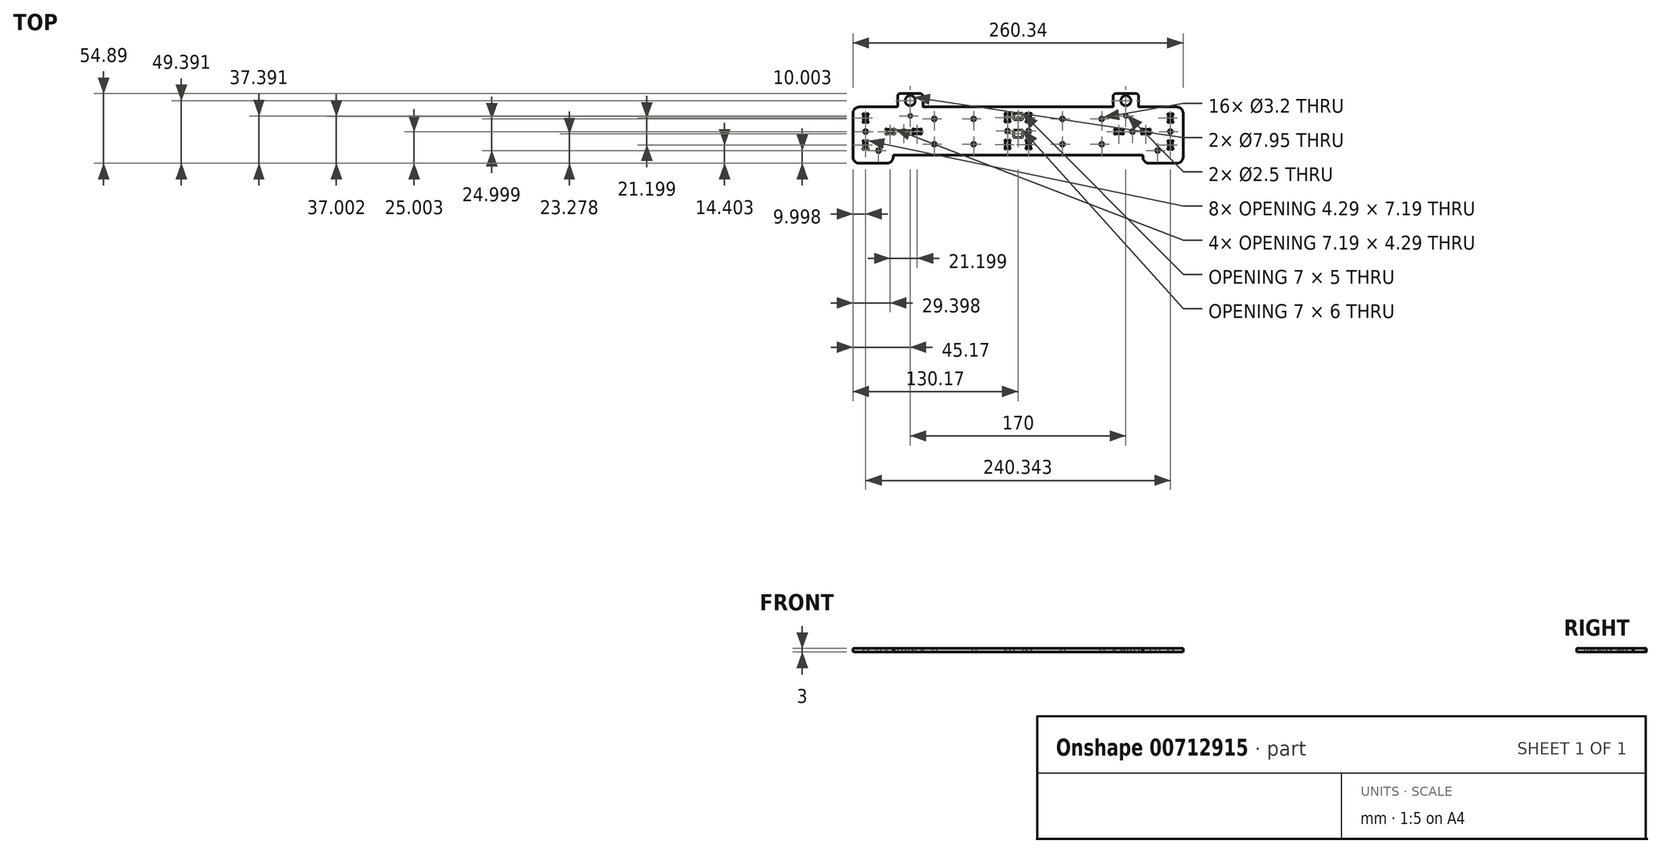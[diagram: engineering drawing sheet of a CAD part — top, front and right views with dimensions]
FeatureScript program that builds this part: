
annotation { "Feature Type Name" : "Feature", "Feature Type Description" : "" }
export const myFeature = defineFeature(function(context is Context, id is Id, definition is map)
    precondition{}
    {
        {
            var Q0;
            Q0=qCreatedBy(makeId("Top.planeOp"),FACE);
            var sketch = newSketch(context, id + "F0", { "sketchPlane" : qUnion([Q0])});
            skArc(sketch, "E0", {"start": v(-130.17, -20.39) * mm, "mid": v(-128.7, -23.92) * mm, "end": v(-125.17, -25.39) * mm});
            skLineSegment(sketch, "E1", {"start": v(-130.17, -20.39) * mm, "end": v(-130.17, 14) * mm});
            skArc(sketch, "E2", {"start": v(-125.17, 19) * mm, "mid": v(-128.7, 17.54) * mm, "end": v(-130.17, 14) * mm});
            skLineSegment(sketch, "E3", {"start": v(-125.17, 19) * mm, "end": v(-95.5, 19) * mm});
            skArc(sketch, "E4", {"start": v(-95.5, 19) * mm, "mid": v(-95.15, 19.15) * mm, "end": v(-95, 19.5) * mm});
            skArc(sketch, "E5", {"start": v(-75, 19.5) * mm, "mid": v(-74.85, 19.15) * mm, "end": v(-74.5, 19) * mm});
            skLineSegment(sketch, "E6", {"start": v(-74.5, 19) * mm, "end": v(74.5, 19) * mm});
            skArc(sketch, "E7", {"start": v(74.5, 19) * mm, "mid": v(74.85, 19.15) * mm, "end": v(75, 19.5) * mm});
            skArc(sketch, "E8", {"start": v(95, 19.5) * mm, "mid": v(95.15, 19.15) * mm, "end": v(95.5, 19) * mm});
            skLineSegment(sketch, "E9", {"start": v(95.5, 19) * mm, "end": v(125.17, 19) * mm});
            skArc(sketch, "E10", {"start": v(130.17, 14) * mm, "mid": v(128.7, 17.54) * mm, "end": v(125.17, 19) * mm});
            skLineSegment(sketch, "E11", {"start": v(130.17, 14) * mm, "end": v(130.17, -20.39) * mm});
            skArc(sketch, "E12", {"start": v(125.17, -25.39) * mm, "mid": v(128.7, -23.92) * mm, "end": v(130.17, -20.39) * mm});
            skArc(sketch, "E13", {"start": v(118.95, -7.64) * mm, "mid": v(119.14, -7.82) * mm, "end": v(119.39, -7.89) * mm});
            skArc(sketch, "E14", {"start": v(118.95, -7.64) * mm, "mid": v(118.17, -7.53) * mm, "end": v(118.27, -8.32) * mm});
            skArc(sketch, "E15", {"start": v(118.52, -8.75) * mm, "mid": v(118.45, -8.5) * mm, "end": v(118.27, -8.32) * mm});
            skLineSegment(sketch, "E16", {"start": v(118.52, -8.75) * mm, "end": v(118.52, -13.22) * mm});
            skArc(sketch, "E17", {"start": v(118.27, -13.65) * mm, "mid": v(118.45, -13.47) * mm, "end": v(118.52, -13.22) * mm});
            skArc(sketch, "E18", {"start": v(118.27, -13.65) * mm, "mid": v(118.17, -14.44) * mm, "end": v(118.95, -14.34) * mm});
            skArc(sketch, "E19", {"start": v(119.39, -14.09) * mm, "mid": v(119.14, -14.15) * mm, "end": v(118.95, -14.34) * mm});
            skLineSegment(sketch, "E20", {"start": v(119.39, -14.09) * mm, "end": v(120.96, -14.09) * mm});
            skArc(sketch, "E21", {"start": v(121.39, -14.34) * mm, "mid": v(121.2, -14.15) * mm, "end": v(120.96, -14.09) * mm});
            skArc(sketch, "E22", {"start": v(121.39, -14.34) * mm, "mid": v(122.17, -14.44) * mm, "end": v(122.07, -13.65) * mm});
            skArc(sketch, "E23", {"start": v(121.82, -13.22) * mm, "mid": v(121.89, -13.47) * mm, "end": v(122.07, -13.65) * mm});
            skLineSegment(sketch, "E24", {"start": v(121.82, -13.22) * mm, "end": v(121.82, -8.75) * mm});
            skArc(sketch, "E25", {"start": v(122.07, -8.32) * mm, "mid": v(121.89, -8.5) * mm, "end": v(121.82, -8.75) * mm});
            skArc(sketch, "E26", {"start": v(122.07, -8.32) * mm, "mid": v(122.17, -7.53) * mm, "end": v(121.39, -7.64) * mm});
            skArc(sketch, "E27", {"start": v(120.96, -7.89) * mm, "mid": v(121.2, -7.82) * mm, "end": v(121.39, -7.64) * mm});
            skLineSegment(sketch, "E28", {"start": v(120.96, -7.89) * mm, "end": v(119.39, -7.89) * mm});
            skArc(sketch, "E29", {"start": v(118.95, 13.56) * mm, "mid": v(119.14, 13.38) * mm, "end": v(119.39, 13.31) * mm});
            skArc(sketch, "E30", {"start": v(118.95, 13.56) * mm, "mid": v(118.17, 13.67) * mm, "end": v(118.27, 12.88) * mm});
            skArc(sketch, "E31", {"start": v(118.52, 12.45) * mm, "mid": v(118.45, 12.7) * mm, "end": v(118.27, 12.88) * mm});
            skLineSegment(sketch, "E32", {"start": v(118.52, 12.45) * mm, "end": v(118.52, 7.98) * mm});
            skArc(sketch, "E33", {"start": v(118.27, 7.55) * mm, "mid": v(118.45, 7.73) * mm, "end": v(118.52, 7.98) * mm});
            skArc(sketch, "E34", {"start": v(118.27, 7.55) * mm, "mid": v(118.17, 6.76) * mm, "end": v(118.95, 6.86) * mm});
            skArc(sketch, "E35", {"start": v(119.39, 7.11) * mm, "mid": v(119.14, 7.05) * mm, "end": v(118.95, 6.86) * mm});
            skLineSegment(sketch, "E36", {"start": v(119.39, 7.11) * mm, "end": v(120.96, 7.11) * mm});
            skArc(sketch, "E37", {"start": v(121.39, 6.86) * mm, "mid": v(121.2, 7.05) * mm, "end": v(120.96, 7.11) * mm});
            skArc(sketch, "E38", {"start": v(121.39, 6.86) * mm, "mid": v(122.17, 6.76) * mm, "end": v(122.07, 7.55) * mm});
            skArc(sketch, "E39", {"start": v(121.82, 7.98) * mm, "mid": v(121.89, 7.73) * mm, "end": v(122.07, 7.55) * mm});
            skLineSegment(sketch, "E40", {"start": v(121.82, 7.98) * mm, "end": v(121.82, 12.45) * mm});
            skArc(sketch, "E41", {"start": v(122.07, 12.88) * mm, "mid": v(121.89, 12.7) * mm, "end": v(121.82, 12.45) * mm});
            skArc(sketch, "E42", {"start": v(122.07, 12.88) * mm, "mid": v(122.17, 13.67) * mm, "end": v(121.39, 13.56) * mm});
            skArc(sketch, "E43", {"start": v(120.96, 13.31) * mm, "mid": v(121.2, 13.38) * mm, "end": v(121.39, 13.56) * mm});
            skLineSegment(sketch, "E44", {"start": v(120.96, 13.31) * mm, "end": v(119.39, 13.31) * mm});
            skArc(sketch, "E45", {"start": v(-119.39, -7.89) * mm, "mid": v(-119.14, -7.82) * mm, "end": v(-118.95, -7.64) * mm});
            skArc(sketch, "E46", {"start": v(-118.27, -8.32) * mm, "mid": v(-118.17, -7.53) * mm, "end": v(-118.95, -7.64) * mm});
            skArc(sketch, "E47", {"start": v(-118.27, -8.32) * mm, "mid": v(-118.45, -8.5) * mm, "end": v(-118.52, -8.75) * mm});
            skLineSegment(sketch, "E48", {"start": v(-118.52, -8.75) * mm, "end": v(-118.52, -13.22) * mm});
            skArc(sketch, "E49", {"start": v(-118.52, -13.22) * mm, "mid": v(-118.45, -13.47) * mm, "end": v(-118.27, -13.65) * mm});
            skArc(sketch, "E50", {"start": v(-118.95, -14.34) * mm, "mid": v(-118.17, -14.44) * mm, "end": v(-118.27, -13.65) * mm});
            skArc(sketch, "E51", {"start": v(-118.95, -14.34) * mm, "mid": v(-119.14, -14.15) * mm, "end": v(-119.39, -14.09) * mm});
            skLineSegment(sketch, "E52", {"start": v(-119.39, -14.09) * mm, "end": v(-120.96, -14.09) * mm});
            skArc(sketch, "E53", {"start": v(-120.96, -14.09) * mm, "mid": v(-121.2, -14.15) * mm, "end": v(-121.39, -14.34) * mm});
            skArc(sketch, "E54", {"start": v(-122.07, -13.65) * mm, "mid": v(-122.17, -14.44) * mm, "end": v(-121.39, -14.34) * mm});
            skArc(sketch, "E55", {"start": v(-122.07, -13.65) * mm, "mid": v(-121.89, -13.47) * mm, "end": v(-121.82, -13.22) * mm});
            skLineSegment(sketch, "E56", {"start": v(-121.82, -13.22) * mm, "end": v(-121.82, -8.75) * mm});
            skArc(sketch, "E57", {"start": v(-121.82, -8.75) * mm, "mid": v(-121.89, -8.5) * mm, "end": v(-122.07, -8.32) * mm});
            skArc(sketch, "E58", {"start": v(-121.39, -7.64) * mm, "mid": v(-122.17, -7.53) * mm, "end": v(-122.07, -8.32) * mm});
            skArc(sketch, "E59", {"start": v(-121.39, -7.64) * mm, "mid": v(-121.2, -7.82) * mm, "end": v(-120.96, -7.89) * mm});
            skLineSegment(sketch, "E60", {"start": v(-120.96, -7.89) * mm, "end": v(-119.39, -7.89) * mm});
            skArc(sketch, "E61", {"start": v(-119.39, 13.31) * mm, "mid": v(-119.14, 13.38) * mm, "end": v(-118.95, 13.56) * mm});
            skArc(sketch, "E62", {"start": v(-118.27, 12.88) * mm, "mid": v(-118.17, 13.67) * mm, "end": v(-118.95, 13.56) * mm});
            skArc(sketch, "E63", {"start": v(-118.27, 12.88) * mm, "mid": v(-118.45, 12.7) * mm, "end": v(-118.52, 12.45) * mm});
            skLineSegment(sketch, "E64", {"start": v(-118.52, 12.45) * mm, "end": v(-118.52, 7.98) * mm});
            skArc(sketch, "E65", {"start": v(-118.52, 7.98) * mm, "mid": v(-118.45, 7.73) * mm, "end": v(-118.27, 7.55) * mm});
            skArc(sketch, "E66", {"start": v(-118.95, 6.86) * mm, "mid": v(-118.17, 6.76) * mm, "end": v(-118.27, 7.55) * mm});
            skArc(sketch, "E67", {"start": v(-118.95, 6.86) * mm, "mid": v(-119.14, 7.05) * mm, "end": v(-119.39, 7.11) * mm});
            skLineSegment(sketch, "E68", {"start": v(-119.39, 7.11) * mm, "end": v(-120.96, 7.11) * mm});
            skArc(sketch, "E69", {"start": v(-120.96, 7.11) * mm, "mid": v(-121.2, 7.05) * mm, "end": v(-121.39, 6.86) * mm});
            skArc(sketch, "E70", {"start": v(-122.07, 7.55) * mm, "mid": v(-122.17, 6.76) * mm, "end": v(-121.39, 6.86) * mm});
            skArc(sketch, "E71", {"start": v(-122.07, 7.55) * mm, "mid": v(-121.89, 7.73) * mm, "end": v(-121.82, 7.98) * mm});
            skLineSegment(sketch, "E72", {"start": v(-121.82, 7.98) * mm, "end": v(-121.82, 12.45) * mm});
            skArc(sketch, "E73", {"start": v(-121.82, 12.45) * mm, "mid": v(-121.89, 12.7) * mm, "end": v(-122.07, 12.88) * mm});
            skArc(sketch, "E74", {"start": v(-121.39, 13.56) * mm, "mid": v(-122.17, 13.67) * mm, "end": v(-122.07, 12.88) * mm});
            skArc(sketch, "E75", {"start": v(-121.39, 13.56) * mm, "mid": v(-121.2, 13.38) * mm, "end": v(-120.96, 13.31) * mm});
            skLineSegment(sketch, "E76", {"start": v(-120.96, 13.31) * mm, "end": v(-119.39, 13.31) * mm});
            skCircle(sketch, "E77", {"center": v(120.17, -0.39) * mm, "radius": 1.6 * mm});
            skCircle(sketch, "E78", {"center": v(66, -10.39) * mm, "radius": 1.6 * mm});
            skCircle(sketch, "E79", {"center": v(66, 9.61) * mm, "radius": 1.6 * mm});
            skCircle(sketch, "E80", {"center": v(35, -10.39) * mm, "radius": 1.6 * mm});
            skCircle(sketch, "E81", {"center": v(35, 9.61) * mm, "radius": 1.6 * mm});
            skCircle(sketch, "E82", {"center": v(-35, -10.39) * mm, "radius": 1.6 * mm});
            skCircle(sketch, "E83", {"center": v(-35, 9.61) * mm, "radius": 1.6 * mm});
            skCircle(sketch, "E84", {"center": v(-66, -10.39) * mm, "radius": 1.6 * mm});
            skCircle(sketch, "E85", {"center": v(-66, 9.61) * mm, "radius": 1.6 * mm});
            skCircle(sketch, "E86", {"center": v(-120.17, -0.39) * mm, "radius": 1.6 * mm});
            skCircle(sketch, "E87", {"center": v(-85, 12) * mm, "radius": 1.25 * mm});
            skCircle(sketch, "E88", {"center": v(85, 12) * mm, "radius": 1.25 * mm});
            skArc(sketch, "E89", {"start": v(-97.42, 0.83) * mm, "mid": v(-97.6, 0.65) * mm, "end": v(-97.67, 0.4) * mm});
            skArc(sketch, "E90", {"start": v(-97.42, 0.83) * mm, "mid": v(-97.32, 1.62) * mm, "end": v(-98.1, 1.51) * mm});
            skArc(sketch, "E91", {"start": v(-98.54, 1.26) * mm, "mid": v(-98.29, 1.33) * mm, "end": v(-98.1, 1.51) * mm});
            skLineSegment(sketch, "E92", {"start": v(-98.54, 1.26) * mm, "end": v(-103, 1.26) * mm});
            skArc(sketch, "E93", {"start": v(-103.44, 1.51) * mm, "mid": v(-103.26, 1.33) * mm, "end": v(-103, 1.26) * mm});
            skArc(sketch, "E94", {"start": v(-103.44, 1.51) * mm, "mid": v(-104.23, 1.62) * mm, "end": v(-104.12, 0.83) * mm});
            skArc(sketch, "E95", {"start": v(-103.87, 0.4) * mm, "mid": v(-103.94, 0.65) * mm, "end": v(-104.12, 0.83) * mm});
            skLineSegment(sketch, "E96", {"start": v(-103.87, 0.4) * mm, "end": v(-103.87, -1.17) * mm});
            skArc(sketch, "E97", {"start": v(-104.12, -1.6) * mm, "mid": v(-103.94, -1.42) * mm, "end": v(-103.87, -1.17) * mm});
            skArc(sketch, "E98", {"start": v(-104.12, -1.6) * mm, "mid": v(-104.23, -2.4) * mm, "end": v(-103.44, -2.29) * mm});
            skArc(sketch, "E99", {"start": v(-103, -2.04) * mm, "mid": v(-103.26, -2.1) * mm, "end": v(-103.44, -2.29) * mm});
            skLineSegment(sketch, "E100", {"start": v(-103, -2.04) * mm, "end": v(-98.54, -2.04) * mm});
            skArc(sketch, "E101", {"start": v(-98.1, -2.29) * mm, "mid": v(-98.29, -2.1) * mm, "end": v(-98.54, -2.04) * mm});
            skArc(sketch, "E102", {"start": v(-98.1, -2.29) * mm, "mid": v(-97.32, -2.4) * mm, "end": v(-97.42, -1.6) * mm});
            skArc(sketch, "E103", {"start": v(-97.67, -1.17) * mm, "mid": v(-97.6, -1.42) * mm, "end": v(-97.42, -1.6) * mm});
            skLineSegment(sketch, "E104", {"start": v(-97.67, -1.17) * mm, "end": v(-97.67, 0.4) * mm});
            skArc(sketch, "E105", {"start": v(-76.22, 0.83) * mm, "mid": v(-76.4, 0.65) * mm, "end": v(-76.47, 0.4) * mm});
            skArc(sketch, "E106", {"start": v(-76.22, 0.83) * mm, "mid": v(-76.12, 1.62) * mm, "end": v(-76.9, 1.51) * mm});
            skArc(sketch, "E107", {"start": v(-77.34, 1.26) * mm, "mid": v(-77.09, 1.33) * mm, "end": v(-76.9, 1.51) * mm});
            skLineSegment(sketch, "E108", {"start": v(-77.34, 1.26) * mm, "end": v(-81.8, 1.26) * mm});
            skArc(sketch, "E109", {"start": v(-82.24, 1.51) * mm, "mid": v(-82.06, 1.33) * mm, "end": v(-81.8, 1.26) * mm});
            skArc(sketch, "E110", {"start": v(-82.24, 1.51) * mm, "mid": v(-83.03, 1.62) * mm, "end": v(-82.92, 0.83) * mm});
            skArc(sketch, "E111", {"start": v(-82.67, 0.4) * mm, "mid": v(-82.74, 0.65) * mm, "end": v(-82.92, 0.83) * mm});
            skLineSegment(sketch, "E112", {"start": v(-82.67, 0.4) * mm, "end": v(-82.67, -1.17) * mm});
            skArc(sketch, "E113", {"start": v(-82.92, -1.6) * mm, "mid": v(-82.74, -1.42) * mm, "end": v(-82.67, -1.17) * mm});
            skArc(sketch, "E114", {"start": v(-82.92, -1.6) * mm, "mid": v(-83.03, -2.4) * mm, "end": v(-82.24, -2.29) * mm});
            skArc(sketch, "E115", {"start": v(-81.8, -2.04) * mm, "mid": v(-82.06, -2.1) * mm, "end": v(-82.24, -2.29) * mm});
            skLineSegment(sketch, "E116", {"start": v(-81.8, -2.04) * mm, "end": v(-77.34, -2.04) * mm});
            skArc(sketch, "E117", {"start": v(-76.9, -2.29) * mm, "mid": v(-77.09, -2.1) * mm, "end": v(-77.34, -2.04) * mm});
            skArc(sketch, "E118", {"start": v(-76.9, -2.29) * mm, "mid": v(-76.12, -2.4) * mm, "end": v(-76.22, -1.6) * mm});
            skArc(sketch, "E119", {"start": v(-76.47, -1.17) * mm, "mid": v(-76.4, -1.42) * mm, "end": v(-76.22, -1.6) * mm});
            skLineSegment(sketch, "E120", {"start": v(-76.47, -1.17) * mm, "end": v(-76.47, 0.4) * mm});
            skCircle(sketch, "E121", {"center": v(-90.17, -0.39) * mm, "radius": 1.6 * mm});
            skArc(sketch, "E122", {"start": v(82.92, 0.83) * mm, "mid": v(82.74, 0.65) * mm, "end": v(82.67, 0.4) * mm});
            skArc(sketch, "E123", {"start": v(82.92, 0.83) * mm, "mid": v(83.03, 1.62) * mm, "end": v(82.24, 1.51) * mm});
            skArc(sketch, "E124", {"start": v(81.8, 1.26) * mm, "mid": v(82.06, 1.33) * mm, "end": v(82.24, 1.51) * mm});
            skLineSegment(sketch, "E125", {"start": v(81.8, 1.26) * mm, "end": v(77.34, 1.26) * mm});
            skArc(sketch, "E126", {"start": v(76.9, 1.51) * mm, "mid": v(77.09, 1.33) * mm, "end": v(77.34, 1.26) * mm});
            skArc(sketch, "E127", {"start": v(76.9, 1.51) * mm, "mid": v(76.12, 1.62) * mm, "end": v(76.22, 0.83) * mm});
            skArc(sketch, "E128", {"start": v(76.47, 0.4) * mm, "mid": v(76.4, 0.65) * mm, "end": v(76.22, 0.83) * mm});
            skLineSegment(sketch, "E129", {"start": v(76.47, 0.4) * mm, "end": v(76.47, -1.17) * mm});
            skArc(sketch, "E130", {"start": v(76.22, -1.6) * mm, "mid": v(76.4, -1.42) * mm, "end": v(76.47, -1.17) * mm});
            skArc(sketch, "E131", {"start": v(76.22, -1.6) * mm, "mid": v(76.12, -2.4) * mm, "end": v(76.9, -2.29) * mm});
            skArc(sketch, "E132", {"start": v(77.34, -2.04) * mm, "mid": v(77.09, -2.1) * mm, "end": v(76.9, -2.29) * mm});
            skLineSegment(sketch, "E133", {"start": v(77.34, -2.04) * mm, "end": v(81.8, -2.04) * mm});
            skArc(sketch, "E134", {"start": v(82.24, -2.29) * mm, "mid": v(82.06, -2.1) * mm, "end": v(81.8, -2.04) * mm});
            skArc(sketch, "E135", {"start": v(82.24, -2.29) * mm, "mid": v(83.03, -2.4) * mm, "end": v(82.92, -1.6) * mm});
            skArc(sketch, "E136", {"start": v(82.67, -1.17) * mm, "mid": v(82.74, -1.42) * mm, "end": v(82.92, -1.6) * mm});
            skLineSegment(sketch, "E137", {"start": v(82.67, -1.17) * mm, "end": v(82.67, 0.4) * mm});
            skArc(sketch, "E138", {"start": v(104.12, 0.83) * mm, "mid": v(103.94, 0.65) * mm, "end": v(103.87, 0.4) * mm});
            skArc(sketch, "E139", {"start": v(104.12, 0.83) * mm, "mid": v(104.23, 1.62) * mm, "end": v(103.44, 1.51) * mm});
            skArc(sketch, "E140", {"start": v(103, 1.26) * mm, "mid": v(103.26, 1.33) * mm, "end": v(103.44, 1.51) * mm});
            skLineSegment(sketch, "E141", {"start": v(103, 1.26) * mm, "end": v(98.54, 1.26) * mm});
            skArc(sketch, "E142", {"start": v(98.1, 1.51) * mm, "mid": v(98.29, 1.33) * mm, "end": v(98.54, 1.26) * mm});
            skArc(sketch, "E143", {"start": v(98.1, 1.51) * mm, "mid": v(97.32, 1.62) * mm, "end": v(97.42, 0.83) * mm});
            skArc(sketch, "E144", {"start": v(97.67, 0.4) * mm, "mid": v(97.6, 0.65) * mm, "end": v(97.42, 0.83) * mm});
            skLineSegment(sketch, "E145", {"start": v(97.67, 0.4) * mm, "end": v(97.67, -1.17) * mm});
            skArc(sketch, "E146", {"start": v(97.42, -1.6) * mm, "mid": v(97.6, -1.42) * mm, "end": v(97.67, -1.17) * mm});
            skArc(sketch, "E147", {"start": v(97.42, -1.6) * mm, "mid": v(97.32, -2.4) * mm, "end": v(98.1, -2.29) * mm});
            skArc(sketch, "E148", {"start": v(98.54, -2.04) * mm, "mid": v(98.29, -2.1) * mm, "end": v(98.1, -2.29) * mm});
            skLineSegment(sketch, "E149", {"start": v(98.54, -2.04) * mm, "end": v(103, -2.04) * mm});
            skArc(sketch, "E150", {"start": v(103.44, -2.29) * mm, "mid": v(103.26, -2.1) * mm, "end": v(103, -2.04) * mm});
            skArc(sketch, "E151", {"start": v(103.44, -2.29) * mm, "mid": v(104.23, -2.4) * mm, "end": v(104.12, -1.6) * mm});
            skArc(sketch, "E152", {"start": v(103.87, -1.17) * mm, "mid": v(103.94, -1.42) * mm, "end": v(104.12, -1.6) * mm});
            skLineSegment(sketch, "E153", {"start": v(103.87, -1.17) * mm, "end": v(103.87, 0.4) * mm});
            skCircle(sketch, "E154", {"center": v(90.17, -0.39) * mm, "radius": 1.6 * mm});
            skLineSegment(sketch, "E155", {"start": v(-103.44, -25.39) * mm, "end": v(-125.17, -25.39) * mm});
            skArc(sketch, "E156", {"start": v(-103.44, -25.39) * mm, "mid": v(-99.9, -23.92) * mm, "end": v(-98.44, -20.39) * mm});
            skLineSegment(sketch, "E157", {"start": v(125.17, -25.39) * mm, "end": v(103.44, -25.39) * mm});
            skArc(sketch, "E158", {"start": v(98.44, -20.39) * mm, "mid": v(99.9, -23.92) * mm, "end": v(103.44, -25.39) * mm});
            skLineSegment(sketch, "E159", {"start": v(-98.44, -20.39) * mm, "end": v(-98.44, -19.5) * mm});
            skArc(sketch, "E160", {"start": v(-97.94, -19) * mm, "mid": v(-98.3, -19.15) * mm, "end": v(-98.44, -19.5) * mm});
            skLineSegment(sketch, "E161", {"start": v(98.44, -20.39) * mm, "end": v(98.44, -19.5) * mm});
            skLineSegment(sketch, "E162", {"start": v(-97.94, -19) * mm, "end": v(97.94, -19) * mm});
            skArc(sketch, "E163", {"start": v(98.44, -19.5) * mm, "mid": v(98.3, -19.15) * mm, "end": v(97.94, -19) * mm});
            skCircle(sketch, "E164", {"center": v(-8.3, 0) * mm, "radius": 1.6 * mm});
            skArc(sketch, "E165", {"start": v(-9.52, -7.25) * mm, "mid": v(-9.33, -7.43) * mm, "end": v(-9.08, -7.5) * mm});
            skArc(sketch, "E166", {"start": v(-9.52, -7.25) * mm, "mid": v(-10.3, -7.15) * mm, "end": v(-10.2, -7.93) * mm});
            skArc(sketch, "E167", {"start": v(-9.95, -8.37) * mm, "mid": v(-10.02, -8.12) * mm, "end": v(-10.2, -7.93) * mm});
            skLineSegment(sketch, "E168", {"start": v(-9.95, -8.37) * mm, "end": v(-9.95, -12.83) * mm});
            skArc(sketch, "E169", {"start": v(-10.2, -13.27) * mm, "mid": v(-10.02, -13.08) * mm, "end": v(-9.95, -12.83) * mm});
            skArc(sketch, "E170", {"start": v(-10.2, -13.27) * mm, "mid": v(-10.3, -14.05) * mm, "end": v(-9.52, -13.95) * mm});
            skArc(sketch, "E171", {"start": v(-9.08, -13.7) * mm, "mid": v(-9.33, -13.77) * mm, "end": v(-9.52, -13.95) * mm});
            skLineSegment(sketch, "E172", {"start": v(-9.08, -13.7) * mm, "end": v(-7.52, -13.7) * mm});
            skArc(sketch, "E173", {"start": v(-7.08, -13.95) * mm, "mid": v(-7.27, -13.77) * mm, "end": v(-7.52, -13.7) * mm});
            skArc(sketch, "E174", {"start": v(-7.08, -13.95) * mm, "mid": v(-6.3, -14.05) * mm, "end": v(-6.4, -13.27) * mm});
            skArc(sketch, "E175", {"start": v(-6.65, -12.83) * mm, "mid": v(-6.58, -13.08) * mm, "end": v(-6.4, -13.27) * mm});
            skLineSegment(sketch, "E176", {"start": v(-6.65, -12.83) * mm, "end": v(-6.65, -8.37) * mm});
            skArc(sketch, "E177", {"start": v(-6.4, -7.93) * mm, "mid": v(-6.58, -8.12) * mm, "end": v(-6.65, -8.37) * mm});
            skArc(sketch, "E178", {"start": v(-6.4, -7.93) * mm, "mid": v(-6.3, -7.15) * mm, "end": v(-7.08, -7.25) * mm});
            skArc(sketch, "E179", {"start": v(-7.52, -7.5) * mm, "mid": v(-7.27, -7.43) * mm, "end": v(-7.08, -7.25) * mm});
            skLineSegment(sketch, "E180", {"start": v(-7.52, -7.5) * mm, "end": v(-9.08, -7.5) * mm});
            skArc(sketch, "E181", {"start": v(-9.52, 13.95) * mm, "mid": v(-9.33, 13.77) * mm, "end": v(-9.08, 13.7) * mm});
            skArc(sketch, "E182", {"start": v(-9.52, 13.95) * mm, "mid": v(-10.3, 14.05) * mm, "end": v(-10.2, 13.27) * mm});
            skArc(sketch, "E183", {"start": v(-9.95, 12.83) * mm, "mid": v(-10.02, 13.08) * mm, "end": v(-10.2, 13.27) * mm});
            skLineSegment(sketch, "E184", {"start": v(-9.95, 12.83) * mm, "end": v(-9.95, 8.37) * mm});
            skArc(sketch, "E185", {"start": v(-10.2, 7.93) * mm, "mid": v(-10.02, 8.12) * mm, "end": v(-9.95, 8.37) * mm});
            skArc(sketch, "E186", {"start": v(-10.2, 7.93) * mm, "mid": v(-10.3, 7.15) * mm, "end": v(-9.52, 7.25) * mm});
            skArc(sketch, "E187", {"start": v(-9.08, 7.5) * mm, "mid": v(-9.33, 7.43) * mm, "end": v(-9.52, 7.25) * mm});
            skLineSegment(sketch, "E188", {"start": v(-9.08, 7.5) * mm, "end": v(-7.52, 7.5) * mm});
            skArc(sketch, "E189", {"start": v(-7.08, 7.25) * mm, "mid": v(-7.27, 7.43) * mm, "end": v(-7.52, 7.5) * mm});
            skArc(sketch, "E190", {"start": v(-7.08, 7.25) * mm, "mid": v(-6.3, 7.15) * mm, "end": v(-6.4, 7.93) * mm});
            skArc(sketch, "E191", {"start": v(-6.65, 8.37) * mm, "mid": v(-6.58, 8.12) * mm, "end": v(-6.4, 7.93) * mm});
            skLineSegment(sketch, "E192", {"start": v(-6.65, 8.37) * mm, "end": v(-6.65, 12.83) * mm});
            skArc(sketch, "E193", {"start": v(-6.4, 13.27) * mm, "mid": v(-6.58, 13.08) * mm, "end": v(-6.65, 12.83) * mm});
            skArc(sketch, "E194", {"start": v(-6.4, 13.27) * mm, "mid": v(-6.3, 14.05) * mm, "end": v(-7.08, 13.95) * mm});
            skArc(sketch, "E195", {"start": v(-7.52, 13.7) * mm, "mid": v(-7.27, 13.77) * mm, "end": v(-7.08, 13.95) * mm});
            skLineSegment(sketch, "E196", {"start": v(-7.52, 13.7) * mm, "end": v(-9.08, 13.7) * mm});
            skCircle(sketch, "E197", {"center": v(8.3, 0) * mm, "radius": 1.6 * mm});
            skArc(sketch, "E198", {"start": v(7.08, -7.25) * mm, "mid": v(7.27, -7.43) * mm, "end": v(7.52, -7.5) * mm});
            skArc(sketch, "E199", {"start": v(7.08, -7.25) * mm, "mid": v(6.3, -7.15) * mm, "end": v(6.4, -7.93) * mm});
            skArc(sketch, "E200", {"start": v(6.65, -8.37) * mm, "mid": v(6.58, -8.12) * mm, "end": v(6.4, -7.93) * mm});
            skLineSegment(sketch, "E201", {"start": v(6.65, -8.37) * mm, "end": v(6.65, -12.83) * mm});
            skArc(sketch, "E202", {"start": v(6.4, -13.27) * mm, "mid": v(6.58, -13.08) * mm, "end": v(6.65, -12.83) * mm});
            skArc(sketch, "E203", {"start": v(6.4, -13.27) * mm, "mid": v(6.3, -14.05) * mm, "end": v(7.08, -13.95) * mm});
            skArc(sketch, "E204", {"start": v(7.52, -13.7) * mm, "mid": v(7.27, -13.77) * mm, "end": v(7.08, -13.95) * mm});
            skLineSegment(sketch, "E205", {"start": v(7.52, -13.7) * mm, "end": v(9.08, -13.7) * mm});
            skArc(sketch, "E206", {"start": v(9.52, -13.95) * mm, "mid": v(9.33, -13.77) * mm, "end": v(9.08, -13.7) * mm});
            skArc(sketch, "E207", {"start": v(9.52, -13.95) * mm, "mid": v(10.3, -14.05) * mm, "end": v(10.2, -13.27) * mm});
            skArc(sketch, "E208", {"start": v(9.95, -12.83) * mm, "mid": v(10.02, -13.08) * mm, "end": v(10.2, -13.27) * mm});
            skLineSegment(sketch, "E209", {"start": v(9.95, -12.83) * mm, "end": v(9.95, -8.37) * mm});
            skArc(sketch, "E210", {"start": v(10.2, -7.93) * mm, "mid": v(10.02, -8.12) * mm, "end": v(9.95, -8.37) * mm});
            skArc(sketch, "E211", {"start": v(10.2, -7.93) * mm, "mid": v(10.3, -7.15) * mm, "end": v(9.52, -7.25) * mm});
            skArc(sketch, "E212", {"start": v(9.08, -7.5) * mm, "mid": v(9.33, -7.43) * mm, "end": v(9.52, -7.25) * mm});
            skLineSegment(sketch, "E213", {"start": v(9.08, -7.5) * mm, "end": v(7.52, -7.5) * mm});
            skArc(sketch, "E214", {"start": v(7.08, 13.95) * mm, "mid": v(7.27, 13.77) * mm, "end": v(7.52, 13.7) * mm});
            skArc(sketch, "E215", {"start": v(7.08, 13.95) * mm, "mid": v(6.3, 14.05) * mm, "end": v(6.4, 13.27) * mm});
            skArc(sketch, "E216", {"start": v(6.65, 12.83) * mm, "mid": v(6.58, 13.08) * mm, "end": v(6.4, 13.27) * mm});
            skLineSegment(sketch, "E217", {"start": v(6.65, 12.83) * mm, "end": v(6.65, 8.37) * mm});
            skArc(sketch, "E218", {"start": v(6.4, 7.93) * mm, "mid": v(6.58, 8.12) * mm, "end": v(6.65, 8.37) * mm});
            skArc(sketch, "E219", {"start": v(6.4, 7.93) * mm, "mid": v(6.3, 7.15) * mm, "end": v(7.08, 7.25) * mm});
            skArc(sketch, "E220", {"start": v(7.52, 7.5) * mm, "mid": v(7.27, 7.43) * mm, "end": v(7.08, 7.25) * mm});
            skLineSegment(sketch, "E221", {"start": v(7.52, 7.5) * mm, "end": v(9.08, 7.5) * mm});
            skArc(sketch, "E222", {"start": v(9.52, 7.25) * mm, "mid": v(9.33, 7.43) * mm, "end": v(9.08, 7.5) * mm});
            skArc(sketch, "E223", {"start": v(9.52, 7.25) * mm, "mid": v(10.3, 7.15) * mm, "end": v(10.2, 7.93) * mm});
            skArc(sketch, "E224", {"start": v(9.95, 8.37) * mm, "mid": v(10.02, 8.12) * mm, "end": v(10.2, 7.93) * mm});
            skLineSegment(sketch, "E225", {"start": v(9.95, 8.37) * mm, "end": v(9.95, 12.83) * mm});
            skArc(sketch, "E226", {"start": v(10.2, 13.27) * mm, "mid": v(10.02, 13.08) * mm, "end": v(9.95, 12.83) * mm});
            skArc(sketch, "E227", {"start": v(10.2, 13.27) * mm, "mid": v(10.3, 14.05) * mm, "end": v(9.52, 13.95) * mm});
            skArc(sketch, "E228", {"start": v(9.08, 13.7) * mm, "mid": v(9.33, 13.77) * mm, "end": v(9.52, 13.95) * mm});
            skLineSegment(sketch, "E229", {"start": v(9.08, 13.7) * mm, "end": v(7.52, 13.7) * mm});
            skCircle(sketch, "E230", {"center": v(-85, 24) * mm, "radius": 3.97 * mm});
            skCircle(sketch, "E231", {"center": v(85, 24) * mm, "radius": 3.97 * mm});
            skLineSegment(sketch, "E232", {"start": v(-95, 19.5) * mm, "end": v(-95, 27.5) * mm});
            skLineSegment(sketch, "E233", {"start": v(-75, 27.5) * mm, "end": v(-75, 19.5) * mm});
            skArc(sketch, "E234", {"start": v(-93, 29.5) * mm, "mid": v(-94.41, 28.92) * mm, "end": v(-95, 27.5) * mm});
            skLineSegment(sketch, "E235", {"start": v(-93, 29.5) * mm, "end": v(-77, 29.5) * mm});
            skArc(sketch, "E236", {"start": v(-75, 27.5) * mm, "mid": v(-75.59, 28.92) * mm, "end": v(-77, 29.5) * mm});
            skLineSegment(sketch, "E237", {"start": v(75, 19.5) * mm, "end": v(75, 27.5) * mm});
            skLineSegment(sketch, "E238", {"start": v(95, 27.5) * mm, "end": v(95, 19.5) * mm});
            skArc(sketch, "E239", {"start": v(77, 29.5) * mm, "mid": v(75.59, 28.92) * mm, "end": v(75, 27.5) * mm});
            skLineSegment(sketch, "E240", {"start": v(77, 29.5) * mm, "end": v(93, 29.5) * mm});
            skArc(sketch, "E241", {"start": v(95, 27.5) * mm, "mid": v(94.41, 28.92) * mm, "end": v(93, 29.5) * mm});
            skArc(sketch, "E242", {"start": v(-3.5, 9.51) * mm, "mid": v(-3.38, 9.23) * mm, "end": v(-3.1, 9.11) * mm});
            skLineSegment(sketch, "E243", {"start": v(3.1, 9.11) * mm, "end": v(-3.1, 9.11) * mm});
            skArc(sketch, "E244", {"start": v(3.1, 9.11) * mm, "mid": v(3.38, 9.23) * mm, "end": v(3.5, 9.51) * mm});
            skArc(sketch, "E245", {"start": v(3.5, 0.49) * mm, "mid": v(3.38, 0.77) * mm, "end": v(3.1, 0.89) * mm});
            skLineSegment(sketch, "E246", {"start": v(-3.1, 0.89) * mm, "end": v(3.1, 0.89) * mm});
            skArc(sketch, "E247", {"start": v(-3.1, 0.89) * mm, "mid": v(-3.38, 0.77) * mm, "end": v(-3.5, 0.49) * mm});
            skArc(sketch, "E248", {"start": v(3.1, -5.11) * mm, "mid": v(3.38, -5) * mm, "end": v(3.5, -4.71) * mm});
            skLineSegment(sketch, "E249", {"start": v(3.1, -5.11) * mm, "end": v(-3.1, -5.11) * mm});
            skArc(sketch, "E250", {"start": v(-3.5, -4.71) * mm, "mid": v(-3.38, -5) * mm, "end": v(-3.1, -5.11) * mm});
            skLineSegment(sketch, "E251", {"start": v(3.5, 0.49) * mm, "end": v(3.5, -4.71) * mm});
            skLineSegment(sketch, "E252", {"start": v(-3.5, -4.71) * mm, "end": v(-3.5, 0.49) * mm});
            skArc(sketch, "E253", {"start": v(-3.1, 14.11) * mm, "mid": v(-3.38, 14) * mm, "end": v(-3.5, 13.71) * mm});
            skLineSegment(sketch, "E254", {"start": v(-3.1, 14.11) * mm, "end": v(3.1, 14.11) * mm});
            skArc(sketch, "E255", {"start": v(3.5, 13.71) * mm, "mid": v(3.38, 14) * mm, "end": v(3.1, 14.11) * mm});
            skLineSegment(sketch, "E256", {"start": v(-3.5, 9.51) * mm, "end": v(-3.5, 13.71) * mm});
            skLineSegment(sketch, "E257", {"start": v(3.5, 13.71) * mm, "end": v(3.5, 9.51) * mm});
            skCircle(sketch, "E258", {"center": v(-110, -15.39) * mm, "radius": 1.6 * mm});
            skCircle(sketch, "E259", {"center": v(110, -15.39) * mm, "radius": 1.6 * mm});
            skSolve(sketch);
        }
        {
            var Q0;
            Q0=makeQuery(id+"F0.imprint","IMPRINT",FACE,{"disambiguationData":[TD([[makeQuery(id+"F0.imprint","IMPRINT",EDGE,{"derivedFrom":sQuery(id+"F0.wireOp",EDGE,"E0")}),1.0]])]});
            extrude(context, id + "F1", {"entities" : qUnion([Q0]), "depth" : 3 * mm, "offsetDistance" : 25 * mm, "symmetric" : true});
        }
    });
